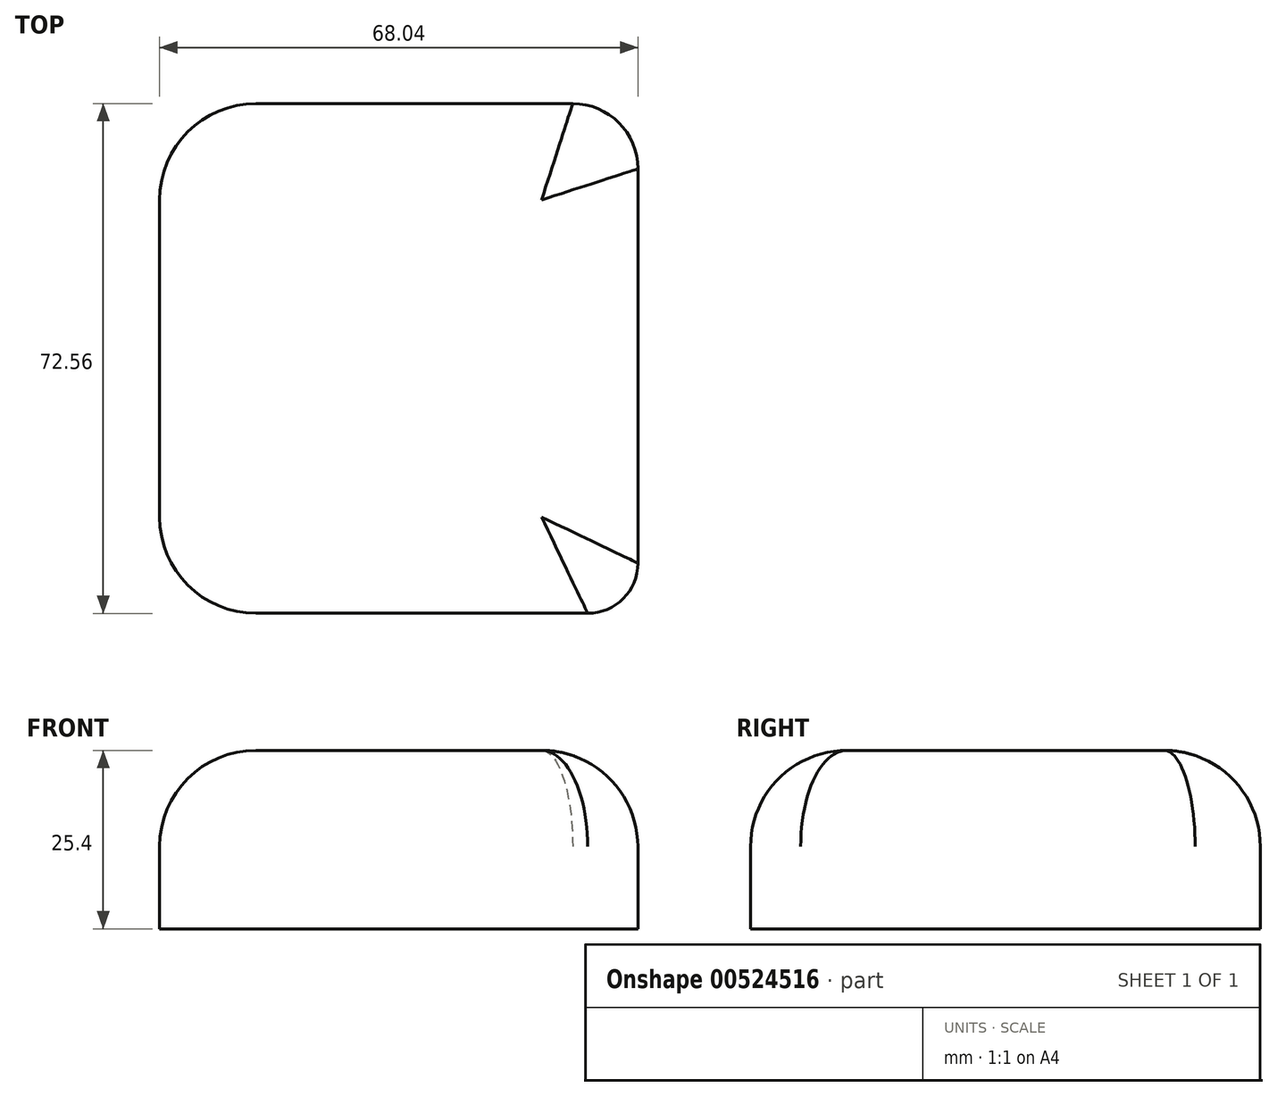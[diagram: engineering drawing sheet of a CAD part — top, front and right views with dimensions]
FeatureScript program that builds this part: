
annotation { "Feature Type Name" : "Feature", "Feature Type Description" : "" }
export const myFeature = defineFeature(function(context is Context, id is Id, definition is map)
    precondition{}
    {
        {
            var Q0;
            Q0=qCreatedBy(makeId("Top.planeOp"),FACE);
            var sketch = newSketch(context, id + "F0", { "sketchPlane" : qUnion([Q0])});
            skLineSegment(sketch, "E0.bottom", {"start": v(34.06, -40.43) * mm, "end": v(-33.98, -40.43) * mm});
            skLineSegment(sketch, "E0.top", {"start": v(34.06, 32.13) * mm, "end": v(-33.98, 32.13) * mm});
            skLineSegment(sketch, "E0.left", {"start": v(34.06, -40.43) * mm, "end": v(34.06, 32.13) * mm});
            skLineSegment(sketch, "E0.right", {"start": v(-33.98, -40.43) * mm, "end": v(-33.98, 32.13) * mm});
            skSolve(sketch);
        }
        {
            var Q0;
            Q0=makeQuery(id+"F0.imprint","IMPRINT",FACE,{"disambiguationData":[TD([[makeQuery(id+"F0.imprint","IMPRINT",EDGE,{"derivedFrom":sQuery(id+"F0.wireOp",EDGE,"E0.bottom")}),-1.0]])]});
            extrude(context, id + "F1", {"entities" : qUnion([Q0]), "depth" : 25.4 * mm, "offsetDistance" : 25.4 * mm});
        }
        {
            var Q0;
            Q0=makeQuery(id+"F1.opExtrude","SWEPT_EDGE",EDGE,{"disambiguationData":[OSD([sQuery(id+"F0.wireOp",EDGE,"E0.bottom"),sQuery(id+"F0.wireOp",EDGE,"E0.left")])]});
            fillet(context, id + "F2", {"entities" : qUnion([Q0]), "radius" : 7.15 * mm, "tangentPropagation" : true, "allowEdgeOverflow" : false});
        }
        {
            var Q0;
            Q0=makeQuery(id+"F1.opExtrude","SWEPT_EDGE",EDGE,{"disambiguationData":[OSD([sQuery(id+"F0.wireOp",EDGE,"E0.top"),sQuery(id+"F0.wireOp",EDGE,"E0.left")])]});
            fillet(context, id + "F3", {"entities" : qUnion([Q0]), "radius" : 9.28 * mm, "tangentPropagation" : true, "allowEdgeOverflow" : false});
        }
        {
            var Q0;
            Q0=makeQuery(id+"F1.opExtrude","SWEPT_EDGE",EDGE,{"disambiguationData":[OSD([sQuery(id+"F0.wireOp",EDGE,"E0.bottom"),sQuery(id+"F0.wireOp",EDGE,"E0.right")])]});
            var Q1;
            Q1=makeQuery(id+"F1.opExtrude","SWEPT_EDGE",EDGE,{"disambiguationData":[OSD([sQuery(id+"F0.wireOp",EDGE,"E0.top"),sQuery(id+"F0.wireOp",EDGE,"E0.right")])]});
            var Q2;
            Q2=makeQuery(id+"F1.opExtrude","CAP_FACE",FACE,{"disambiguationData":[OSD([sQuery(id+"F0.wireOp",EDGE,"E0.bottom"),sQuery(id+"F0.wireOp",EDGE,"E0.top"),sQuery(id+"F0.wireOp",EDGE,"E0.left"),sQuery(id+"F0.wireOp",EDGE,"E0.right")])],"isStart":false});
            fillet(context, id + "F4", {"entities" : qUnion([Q0, Q1, Q2]), "radius" : 13.7 * mm, "tangentPropagation" : true, "allowEdgeOverflow" : false});
        }
    });
